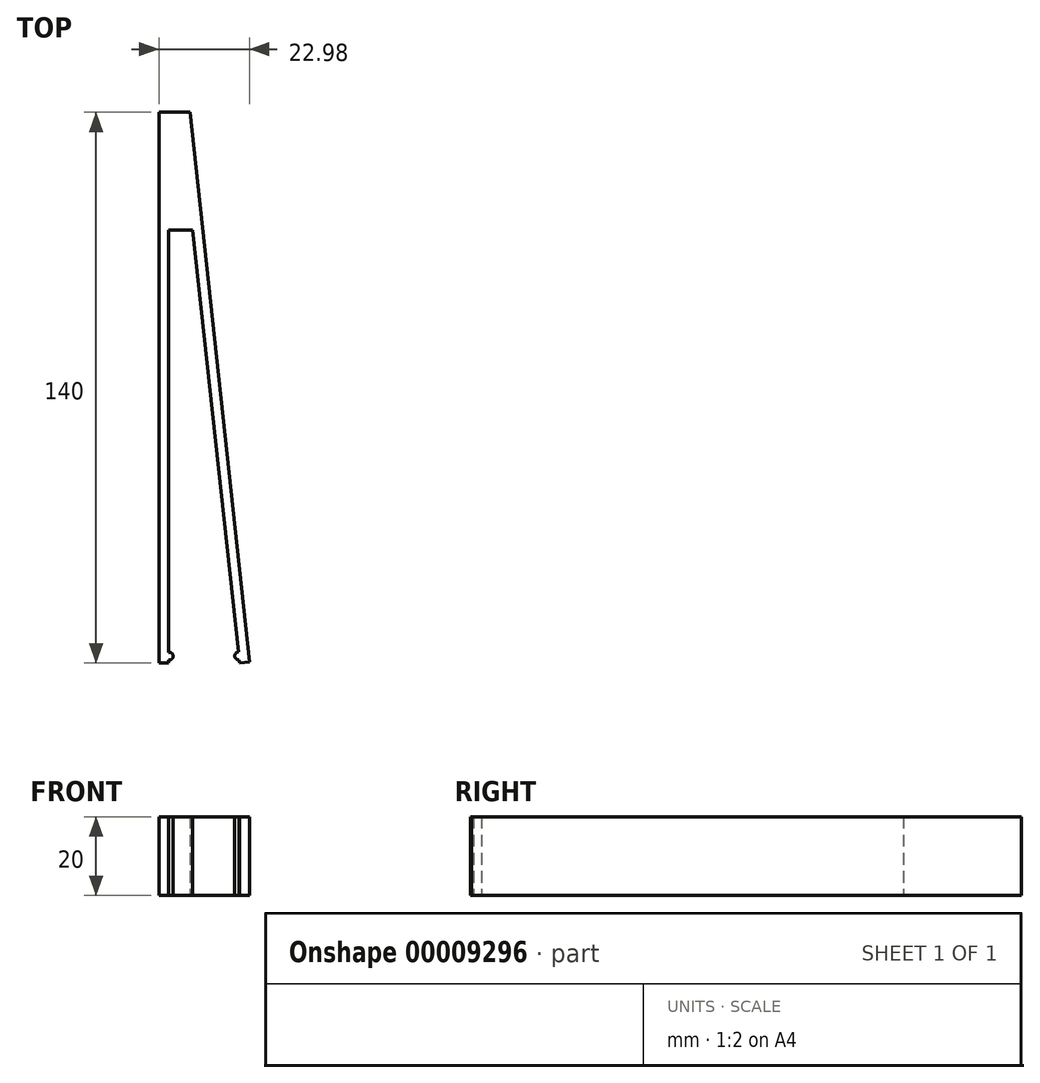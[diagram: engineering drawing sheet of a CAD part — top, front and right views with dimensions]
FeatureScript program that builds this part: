
annotation { "Feature Type Name" : "Feature", "Feature Type Description" : "" }
export const myFeature = defineFeature(function(context is Context, id is Id, definition is map)
    precondition{}
    {
        {
            var Q0;
            Q0=qCreatedBy(makeId("Top.planeOp"),FACE);
            var sketch = newSketch(context, id + "F0", { "sketchPlane" : qUnion([Q0])});
            skLineSegment(sketch, "E0", {"start": v(-23.76, -108.43) * mm, "end": v(-23.76, 31.57) * mm});
            skLineSegment(sketch, "E1", {"start": v(-23.76, 31.57) * mm, "end": v(-21.26, 31.57) * mm});
            skLineSegment(sketch, "E2", {"start": v(-21.26, 31.57) * mm, "end": v(-21.26, -108.43) * mm});
            skLineSegment(sketch, "E3", {"start": v(-21.26, -108.43) * mm, "end": v(-23.76, -108.43) * mm});
            skLineSegment(sketch, "E4", {"start": v(-21.26, 31.57) * mm, "end": v(-18.43, 31.57) * mm});
            skLineSegment(sketch, "E5", {"start": v(-18.43, 31.57) * mm, "end": v(-3.26, -108.43) * mm});
            skLineSegment(sketch, "E6", {"start": v(-3.26, -108.43) * mm, "end": v(-0.78, -108.16) * mm});
            skLineSegment(sketch, "E7", {"start": v(-0.78, -108.16) * mm, "end": v(-15.92, 31.57) * mm});
            skLineSegment(sketch, "E8", {"start": v(-15.92, 31.57) * mm, "end": v(-18.43, 31.57) * mm});
            skLineSegment(sketch, "E9", {"start": v(-21.26, 1.57) * mm, "end": v(-15.18, 1.57) * mm});
            skArc(sketch, "E10", {"start": v(-21.26, -107.64) * mm, "mid": v(-20.18, -106.64) * mm, "end": v(-21.26, -105.65) * mm});
            skArc(sketch, "E11", {"start": v(-3.57, -105.58) * mm, "mid": v(-4.51, -106.68) * mm, "end": v(-3.35, -107.56) * mm});
            skArc(sketch, "E12.0.1.0", {"start": v(-21.29, -104.64) * mm, "mid": v(-20.2, -103.64) * mm, "end": v(-21.29, -102.65) * mm});
            skArc(sketch, "E12.0.2.0", {"start": v(-21.32, -101.64) * mm, "mid": v(-20.23, -100.64) * mm, "end": v(-21.32, -99.65) * mm});
            skLineSegment(sketch, "E12.direction1", {"start": v(-21.26, -107.64) * mm, "end": v(-16.65, -107.53) * mm, "construction": true});
            skLineSegment(sketch, "E12.direction2", {"start": v(-21.26, -107.64) * mm, "end": v(-21.29, -104.64) * mm, "construction": true});
            skArc(sketch, "E13.0.1.0", {"start": v(-3.88, -102.6) * mm, "mid": v(-4.82, -103.7) * mm, "end": v(-3.66, -104.58) * mm});
            skArc(sketch, "E13.0.2.0", {"start": v(-4.18, -99.6) * mm, "mid": v(-5.12, -100.72) * mm, "end": v(-3.97, -101.6) * mm});
            skLineSegment(sketch, "E13.direction1", {"start": v(-3.35, -107.56) * mm, "end": v(1.02, -107.34) * mm, "construction": true});
            skLineSegment(sketch, "E13.direction2", {"start": v(-3.35, -107.56) * mm, "end": v(-3.66, -104.58) * mm, "construction": true});
            skSolve(sketch);
        }
        {
            var Q0;
            {var subQ1=sQuery(id+"F0.wireOp",EDGE,"E6");Q0=makeQuery(id+"F0.imprint","IMPRINT",FACE,{"disambiguationData":[TD([[makeQuery(id+"F0.imprint","IMPRINT",EDGE,{"derivedFrom":subQ1}),1.0]])]});}
            var Q1;
            {var subQ2=sQuery(id+"F0.wireOp",EDGE,"E4");Q1=makeQuery(id+"F0.imprint","IMPRINT",FACE,{"disambiguationData":[TD([[makeQuery(id+"F0.imprint","IMPRINT",EDGE,{"derivedFrom":subQ2}),-1.0]])]});}
            var Q2;
            Q2=makeQuery(id+"F0.imprint","IMPRINT",FACE,{"disambiguationData":[TD([[makeQuery(id+"F0.imprint","IMPRINT",EDGE,{"derivedFrom":sQuery(id+"F0.wireOp",EDGE,"E0")}),-1.0]])]});
            var Q3;
            {var subQ0=sQuery(id+"F0.wireOp",EDGE,"1848bc63-e145-4b45-9d07-776eba10c19a.0.2.0");var subQ1=sQuery(id+"F0.wireOp",EDGE,"E2");var subQ3=makeQuery(id+"F0.imprint","INTERSECT",VERTEX,{"disambiguationData":[OD(0.0)],"derivedFrom":[subQ1,subQ0]});Q3=makeQuery(id+"F0.imprint","IMPRINT",FACE,{"disambiguationData":[TD([[makeQuery(id+"F0.imprint","IMPRINT",EDGE,{"disambiguationData":[TD([[subQ3,-1.0]])],"derivedFrom":subQ1}),1.0]])]});}
            var Q4;
            {var subQ0=sQuery(id+"F0.wireOp",EDGE,"E10");Q4=makeQuery(id+"F0.imprint","IMPRINT",FACE,{"disambiguationData":[TD([[makeQuery(id+"F0.imprint","IMPRINT",EDGE,{"derivedFrom":subQ0}),1.0]])]});}
            var Q5;
            {var subQ0=sQuery(id+"F0.wireOp",EDGE,"1848bc63-e145-4b45-9d07-776eba10c19a.0.1.0");var subQ1=sQuery(id+"F0.wireOp",EDGE,"E2");var subQ3=makeQuery(id+"F0.imprint","INTERSECT",VERTEX,{"disambiguationData":[OD(0.0)],"derivedFrom":[subQ1,subQ0]});Q5=makeQuery(id+"F0.imprint","IMPRINT",FACE,{"disambiguationData":[TD([[makeQuery(id+"F0.imprint","IMPRINT",EDGE,{"disambiguationData":[TD([[subQ3,-1.0]])],"derivedFrom":subQ1}),1.0]])]});}
            var Q6;
            {var subQ0=sQuery(id+"F0.wireOp",EDGE,"E11");Q6=makeQuery(id+"F0.imprint","IMPRINT",FACE,{"disambiguationData":[TD([[makeQuery(id+"F0.imprint","IMPRINT",EDGE,{"derivedFrom":subQ0}),1.0]])]});}
            var Q7;
            {var subQ0=sQuery(id+"F0.wireOp",EDGE,"7cd62e9c-48ec-405c-90f6-d4069c2b3f0a.0.1.0");var subQ1=sQuery(id+"F0.wireOp",EDGE,"E5");var subQ3=makeQuery(id+"F0.imprint","INTERSECT",VERTEX,{"disambiguationData":[OD(0.0)],"derivedFrom":[subQ1,subQ0]});Q7=makeQuery(id+"F0.imprint","IMPRINT",FACE,{"disambiguationData":[TD([[makeQuery(id+"F0.imprint","IMPRINT",EDGE,{"disambiguationData":[TD([[subQ3,-1.0]])],"derivedFrom":subQ1}),-1.0]])]});}
            var Q8;
            {var subQ0=sQuery(id+"F0.wireOp",EDGE,"7cd62e9c-48ec-405c-90f6-d4069c2b3f0a.0.2.0");var subQ1=sQuery(id+"F0.wireOp",EDGE,"E5");var subQ3=makeQuery(id+"F0.imprint","INTERSECT",VERTEX,{"disambiguationData":[OD(0.0)],"derivedFrom":[subQ1,subQ0]});Q8=makeQuery(id+"F0.imprint","IMPRINT",FACE,{"disambiguationData":[TD([[makeQuery(id+"F0.imprint","IMPRINT",EDGE,{"disambiguationData":[TD([[subQ3,-1.0]])],"derivedFrom":subQ1}),-1.0]])]});}
            extrude(context, id + "F1", {"entities" : qUnion([Q0, Q1, Q2, Q3, Q4, Q5, Q6, Q7, Q8]), "depth" : 20 * mm});
        }
    });
